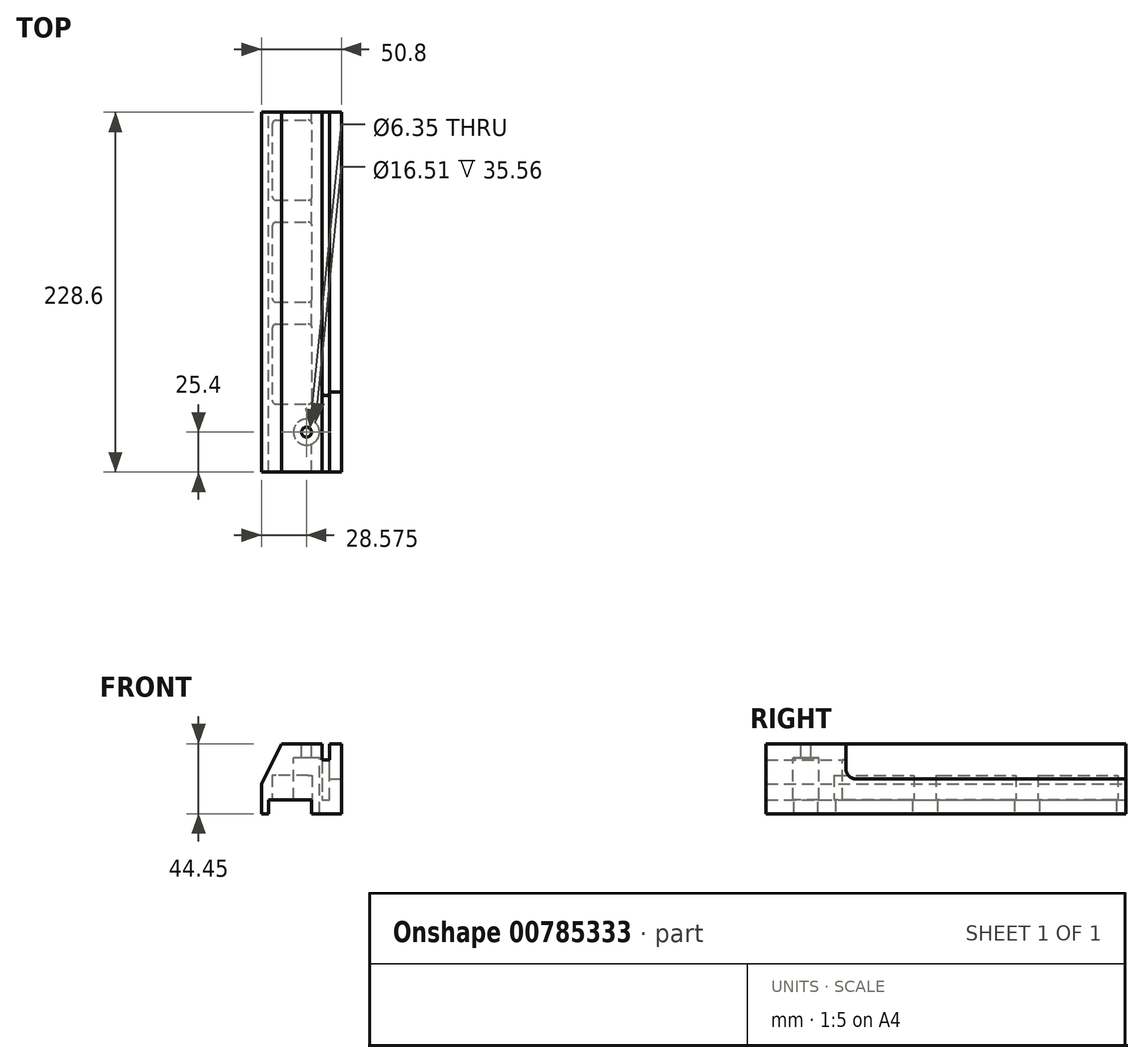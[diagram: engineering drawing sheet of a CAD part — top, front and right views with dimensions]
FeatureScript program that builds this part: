
annotation { "Feature Type Name" : "Feature", "Feature Type Description" : "" }
export const myFeature = defineFeature(function(context is Context, id is Id, definition is map)
    precondition{}
    {
        {
            var Q0;
            Q0=qCreatedBy(makeId("Front.planeOp"),FACE);
            var sketch = newSketch(context, id + "F0", { "sketchPlane" : qUnion([Q0])});
            skLineSegment(sketch, "E0.bottom", {"start": v(0, 0) * mm, "end": v(50.8, 0) * mm});
            skLineSegment(sketch, "E0.top", {"start": v(0, 44.45) * mm, "end": v(50.8, 44.45) * mm});
            skLineSegment(sketch, "E0.left", {"start": v(0, 0) * mm, "end": v(0, 44.45) * mm});
            skLineSegment(sketch, "E0.right", {"start": v(50.8, 0) * mm, "end": v(50.8, 44.45) * mm});
            skSolve(sketch);
        }
        {
            var Q0;
            Q0=qCreatedBy(makeId("Front.planeOp"),FACE);
            var sketch = newSketch(context, id + "F1", { "sketchPlane" : qUnion([Q0])});
            skLineSegment(sketch, "E1.bottom", {"start": v(4.57, 0) * mm, "end": v(31.75, 0) * mm});
            skLineSegment(sketch, "E1.top", {"start": v(4.57, 8.9) * mm, "end": v(31.75, 8.9) * mm});
            skLineSegment(sketch, "E1.left", {"start": v(4.57, 0) * mm, "end": v(4.57, 8.9) * mm});
            skLineSegment(sketch, "E1.right", {"start": v(31.75, 0) * mm, "end": v(31.75, 8.9) * mm});
            skSolve(sketch);
        }
        {
            var Q0;
            Q0=qCreatedBy(makeId("Front.planeOp"),FACE);
            var sketch = newSketch(context, id + "F2", { "sketchPlane" : qUnion([Q0])});
            skLineSegment(sketch, "E2.bottom", {"start": v(38.6, 44.45) * mm, "end": v(43.18, 44.45) * mm});
            skLineSegment(sketch, "E2.top", {"start": v(38.6, 34.3) * mm, "end": v(43.18, 34.3) * mm});
            skLineSegment(sketch, "E2.left", {"start": v(38.6, 44.45) * mm, "end": v(38.6, 34.3) * mm});
            skLineSegment(sketch, "E2.right", {"start": v(43.18, 44.45) * mm, "end": v(43.18, 34.3) * mm});
            skSolve(sketch);
        }
        {
            var Q0;
            Q0 = qSketchRegion(id + "F0", true);
            extrude(context, id + "F3", {"entities" : qUnion([Q0]), "depth" : 228.6 * mm, "offsetDistance" : 25.4 * mm});
        }
        {
            var Q0;
            Q0=makeQuery(id+"F3.opExtrude","SWEPT_EDGE",EDGE,{"disambiguationData":[OSD([sQuery(id+"F0.wireOp",EDGE,"E0.top"),sQuery(id+"F0.wireOp",EDGE,"E0.left")])]});
            chamfer(context, id + "F4", {"entities" : qUnion([Q0]), "chamferType" : ChamferType.TWO_OFFSETS, "width1" : 25.4 * mm, "oppositeDirection" : false, "width2" : 12.7 * mm, "tangentPropagation" : true});
        }
        {
            var Q0;
            Q0 = qSketchRegion(id + "F1", true);
            extrude(context, id + "F5", {"entities" : qUnion([Q0]), "operationType" : NewBodyOperationType.REMOVE, "depth" : 228.6 * mm, "offsetDistance" : 25.4 * mm});
        }
        {
            var Q0;
            Q0 = qSketchRegion(id + "F2", true);
            extrude(context, id + "F6", {"entities" : qUnion([Q0]), "operationType" : NewBodyOperationType.REMOVE, "depth" : 228.6 * mm, "offsetDistance" : 25.4 * mm});
        }
        {
            var Q0;
            {var subQ0=sQuery(id+"F0.wireOp",EDGE,"E0.right");var subQ3=sQuery(id+"F0.wireOp",EDGE,"E0.bottom");Q0=makeQuery(id+"F5.boolean.opBoolean","SPLIT",FACE,{"disambiguationData":[TD([makeQuery(id+"F3.opExtrude","SWEPT_FACE",FACE,{"disambiguationData":[OSD([subQ0])]})])],"derivedFrom":makeQuery(id+"F3.opExtrude","SWEPT_FACE",FACE,{"disambiguationData":[OSD([subQ3])]})});}
            var sketch = newSketch(context, id + "F7", { "sketchPlane" : qUnion([Q0])});
            skLineSegment(sketch, "E3.bottom", {"start": v(29.72, 55.88) * mm, "end": v(9.4, 55.88) * mm});
            skLineSegment(sketch, "E3.top", {"start": v(29.72, 5.08) * mm, "end": v(9.4, 5.08) * mm});
            skLineSegment(sketch, "E3.left", {"start": v(32.26, 53.34) * mm, "end": v(32.26, 7.62) * mm});
            skLineSegment(sketch, "E3.right", {"start": v(6.86, 53.34) * mm, "end": v(6.86, 7.62) * mm});
            skPoint(sketch, "E4.visualSharp", {"position": v(6.86, 55.88) * mm});
            skArc(sketch, "E4.filletArc", {"start": v(9.4, 55.88) * mm, "mid": v(7.6, 55.14) * mm, "end": v(6.86, 53.34) * mm});
            skPoint(sketch, "E5.visualSharp", {"position": v(32.26, 55.88) * mm});
            skArc(sketch, "E5.filletArc", {"start": v(32.26, 53.34) * mm, "mid": v(31.51, 55.14) * mm, "end": v(29.72, 55.88) * mm});
            skPoint(sketch, "E6.visualSharp", {"position": v(32.26, 5.08) * mm});
            skArc(sketch, "E6.filletArc", {"start": v(29.72, 5.08) * mm, "mid": v(31.51, 5.82) * mm, "end": v(32.26, 7.62) * mm});
            skPoint(sketch, "E7.visualSharp", {"position": v(6.86, 5.08) * mm});
            skArc(sketch, "E7.filletArc", {"start": v(6.86, 7.62) * mm, "mid": v(7.6, 5.82) * mm, "end": v(9.4, 5.08) * mm});
            skLineSegment(sketch, "E8.bottom", {"start": v(29.72, 120.65) * mm, "end": v(9.4, 120.65) * mm});
            skLineSegment(sketch, "E8.top", {"start": v(29.72, 69.85) * mm, "end": v(9.4, 69.85) * mm});
            skLineSegment(sketch, "E8.left", {"start": v(32.26, 118.11) * mm, "end": v(32.26, 72.4) * mm});
            skLineSegment(sketch, "E8.right", {"start": v(6.86, 118.11) * mm, "end": v(6.86, 72.4) * mm});
            skPoint(sketch, "E9.visualSharp", {"position": v(6.86, 120.65) * mm});
            skArc(sketch, "E9.filletArc", {"start": v(9.4, 120.65) * mm, "mid": v(7.6, 119.9) * mm, "end": v(6.86, 118.11) * mm});
            skPoint(sketch, "E10.visualSharp", {"position": v(32.26, 120.65) * mm});
            skArc(sketch, "E10.filletArc", {"start": v(32.26, 118.11) * mm, "mid": v(31.51, 119.9) * mm, "end": v(29.72, 120.65) * mm});
            skPoint(sketch, "E11.visualSharp", {"position": v(32.26, 69.85) * mm});
            skArc(sketch, "E11.filletArc", {"start": v(29.72, 69.85) * mm, "mid": v(31.51, 70.6) * mm, "end": v(32.26, 72.4) * mm});
            skPoint(sketch, "E12.visualSharp", {"position": v(6.86, 69.85) * mm});
            skArc(sketch, "E12.filletArc", {"start": v(6.86, 72.4) * mm, "mid": v(7.6, 70.6) * mm, "end": v(9.4, 69.85) * mm});
            skLineSegment(sketch, "E13.bottom", {"start": v(29.72, 185.42) * mm, "end": v(9.4, 185.42) * mm});
            skLineSegment(sketch, "E13.top", {"start": v(29.72, 134.62) * mm, "end": v(9.4, 134.62) * mm});
            skLineSegment(sketch, "E13.left", {"start": v(32.26, 182.88) * mm, "end": v(32.26, 137.16) * mm});
            skLineSegment(sketch, "E13.right", {"start": v(6.86, 182.88) * mm, "end": v(6.86, 137.16) * mm});
            skPoint(sketch, "E14.visualSharp", {"position": v(6.86, 185.42) * mm});
            skArc(sketch, "E14.filletArc", {"start": v(9.4, 185.42) * mm, "mid": v(7.6, 184.68) * mm, "end": v(6.86, 182.88) * mm});
            skPoint(sketch, "E15.visualSharp", {"position": v(32.26, 185.42) * mm});
            skArc(sketch, "E15.filletArc", {"start": v(32.26, 182.88) * mm, "mid": v(31.51, 184.68) * mm, "end": v(29.72, 185.42) * mm});
            skPoint(sketch, "E16.visualSharp", {"position": v(32.26, 134.62) * mm});
            skArc(sketch, "E16.filletArc", {"start": v(29.72, 134.62) * mm, "mid": v(31.51, 135.36) * mm, "end": v(32.26, 137.16) * mm});
            skPoint(sketch, "E17.visualSharp", {"position": v(6.86, 134.62) * mm});
            skArc(sketch, "E17.filletArc", {"start": v(6.86, 137.16) * mm, "mid": v(7.6, 135.36) * mm, "end": v(9.4, 134.62) * mm});
            skSolve(sketch);
        }
        {
            var Q0;
            Q0 = qSketchRegion(id + "F7", true);
            extrude(context, id + "F8", {"entities" : qUnion([Q0]), "operationType" : NewBodyOperationType.REMOVE, "oppositeDirection" : true, "depth" : 24.38 * mm, "offsetDistance" : 25.4 * mm});
        }
        {
            var Q0;
            Q0=makeQuery(id+"F3.opExtrude","SWEPT_FACE",FACE,{"disambiguationData":[OSD([sQuery(id+"F0.wireOp",EDGE,"E0.right")])]});
            var sketch = newSketch(context, id + "F9", { "sketchPlane" : qUnion([Q0])});
            skLineSegment(sketch, "E18.bottom", {"start": v(0, 44.45) * mm, "end": v(-177.8, 44.45) * mm});
            skLineSegment(sketch, "E18.top", {"start": v(0, 22.1) * mm, "end": v(-171.45, 22.1) * mm});
            skLineSegment(sketch, "E18.left", {"start": v(0, 44.45) * mm, "end": v(0, 22.1) * mm});
            skLineSegment(sketch, "E18.right", {"start": v(-177.8, 44.45) * mm, "end": v(-177.8, 28.45) * mm});
            skLineSegment(sketch, "E19.bottom", {"start": v(9.26, 33.5) * mm, "end": v(11.62, 33.5) * mm});
            skLineSegment(sketch, "E19.top", {"start": v(9.26, 34.28) * mm, "end": v(11.62, 34.28) * mm});
            skLineSegment(sketch, "E19.left", {"start": v(9.26, 33.5) * mm, "end": v(9.26, 34.28) * mm});
            skLineSegment(sketch, "E19.right", {"start": v(11.62, 33.5) * mm, "end": v(11.62, 34.28) * mm});
            skPoint(sketch, "E20.visualSharp", {"position": v(-177.8, 22.1) * mm});
            skArc(sketch, "E20.filletArc", {"start": v(-177.8, 28.45) * mm, "mid": v(-175.94, 23.96) * mm, "end": v(-171.45, 22.1) * mm});
            skSolve(sketch);
        }
        {
            var Q0;
            Q0 = qSketchRegion(id + "F9", true);
            extrude(context, id + "F10", {"entities" : qUnion([Q0]), "operationType" : NewBodyOperationType.REMOVE, "oppositeDirection" : true, "depth" : 12.2 * mm, "offsetDistance" : 25.4 * mm});
        }
        {
            var Q0;
            {var subQ2=sQuery(id+"F0.wireOp",EDGE,"E0.top");Q0=makeQuery(id+"F6.boolean.opBoolean","SPLIT",FACE,{"disambiguationData":[TD([makeQuery(id+"F6.opExtrude","SWEPT_FACE",FACE,{"disambiguationData":[OSD([sQuery(id+"F2.wireOp",EDGE,"E2.left")])]})])],"derivedFrom":makeQuery(id+"F3.opExtrude","SWEPT_FACE",FACE,{"disambiguationData":[OSD([subQ2])]})});}
            var sketch = newSketch(context, id + "F11", { "sketchPlane" : qUnion([Q0])});
            skLineSegment(sketch, "E21.bottom", {"start": v(38.6, 0) * mm, "end": v(43.18, 0) * mm});
            skLineSegment(sketch, "E21.top", {"start": v(40.9, -180.09) * mm, "end": v(40.9, -180.09) * mm});
            skLineSegment(sketch, "E21.left", {"start": v(38.6, 0) * mm, "end": v(38.6, -177.8) * mm});
            skLineSegment(sketch, "E21.right", {"start": v(43.18, 0) * mm, "end": v(43.18, -177.8) * mm});
            skPoint(sketch, "E22.visualSharp", {"position": v(38.6, -180.09) * mm});
            skArc(sketch, "E22.filletArc", {"start": v(38.6, -177.8) * mm, "mid": v(39.28, -179.42) * mm, "end": v(40.9, -180.09) * mm});
            skPoint(sketch, "E23.visualSharp", {"position": v(43.18, -180.09) * mm});
            skArc(sketch, "E23.filletArc", {"start": v(40.9, -180.09) * mm, "mid": v(42.51, -179.42) * mm, "end": v(43.18, -177.8) * mm});
            skSolve(sketch);
        }
        {
            var Q0;
            Q0 = qSketchRegion(id + "F11", true);
            extrude(context, id + "F12", {"entities" : qUnion([Q0]), "operationType" : NewBodyOperationType.REMOVE, "oppositeDirection" : true, "depth" : 35.56 * mm, "offsetDistance" : 25.4 * mm});
        }
        {
            var Q0;
            {var subQ0=sQuery(id+"F0.wireOp",EDGE,"E0.right");var subQ3=sQuery(id+"F0.wireOp",EDGE,"E0.bottom");Q0=makeQuery(id+"F5.boolean.opBoolean","SPLIT",FACE,{"disambiguationData":[TD([makeQuery(id+"F3.opExtrude","SWEPT_FACE",FACE,{"disambiguationData":[OSD([subQ0])]})])],"derivedFrom":makeQuery(id+"F3.opExtrude","SWEPT_FACE",FACE,{"disambiguationData":[OSD([subQ3])]})});}
            var sketch = newSketch(context, id + "F13", { "sketchPlane" : qUnion([Q0])});
            skCircle(sketch, "E24", {"center": v(28.58, 203.2) * mm, "radius": 4.2 * mm});
            skSolve(sketch);
        }
        {
            var Q0;
            Q0=sQuery(id+"F13.wireOp",VERTEX,"E24.center");
            var Q1;
            Q1=makeQuery(id+"F3.opExtrude","SWEPT_BODY",BODY,{"disambiguationData":[OSD([sQuery(id+"F0.wireOp",EDGE,"E0.bottom"),sQuery(id+"F0.wireOp",EDGE,"E0.top"),sQuery(id+"F0.wireOp",EDGE,"E0.left"),sQuery(id+"F0.wireOp",EDGE,"E0.right")])]});
            hole(context, id + "F14", {"style" : HoleStyle.C_BORE, "endStyle" : HoleEndStyle.THROUGH, "holeDiameter" : 6.35 * mm, "cBoreDiameter" : 16.5 * mm, "cBoreDepth" : 35.56 * mm, "majorDiameter" : 6.35 * mm, "isTappedThrough" : true, "tappedDepth" : 12.7 * mm, "tapClearance" : 3, "startFromSketch" : true, "locations" : qUnion([Q0]), "scope" : qUnion([Q1])});
        }
    });
